# Revit family: Toilet_Seat-Elongated_Closed_Front-KOHLER-Cymbal-K-57777
name_source: partatom
category: Specialty Equipment
units: mm (PartAtom-declared; Revit-internal decimal feet)

## family parameters
Cut with Voids When Loaded = No
Host = Face
OmniClass Number = 23.31.19.19.17
OmniClass Title = Water Closet Seats
Part Type = Normal
Room Calculation Point = No
Round Connector Dimension = Use Diameter
Shared = No

## types (2) — shared parameters
ADA Compliant = No
Assembly Code = C1030200
Date Modified = 02/18/2024
Default Elevation = 42"
Description = Coreflex Quiet Close Ready Latch Elongated Bowl
Finish = Kohler-Plastic-0-White
Height = 2 3/16"
Length = 20 3/16"
Manufacturer = Kohler Co.
Master Format 2014 = 10 28 00
Master Format 2014 Name = Toilet, Bath, and Laundry Accessories
Material = Plastic
Product Documentation Link = https://www.us.kohler.com
Product Name = Cymbal
Product Page URL = http://www.us.kohler.com
URL = https://www.us.kohler.com
WaterSense Certified = No
Width = 15 1/4"

## per-type parameters (varying)
| type | Model | Secondary Finish | Type |
| GCF, 0-White | K-57777-GCF-0 | Kohler-Plastic-95-Ice_Grey | 1 |
| WCF, 0-White | K-57777-WCF-0 | Kohler-Plastic-0-White | 2 |

## geometry (parser evidence)
native form markers: Sweep x4
no freeform markers — native parametric forms only
